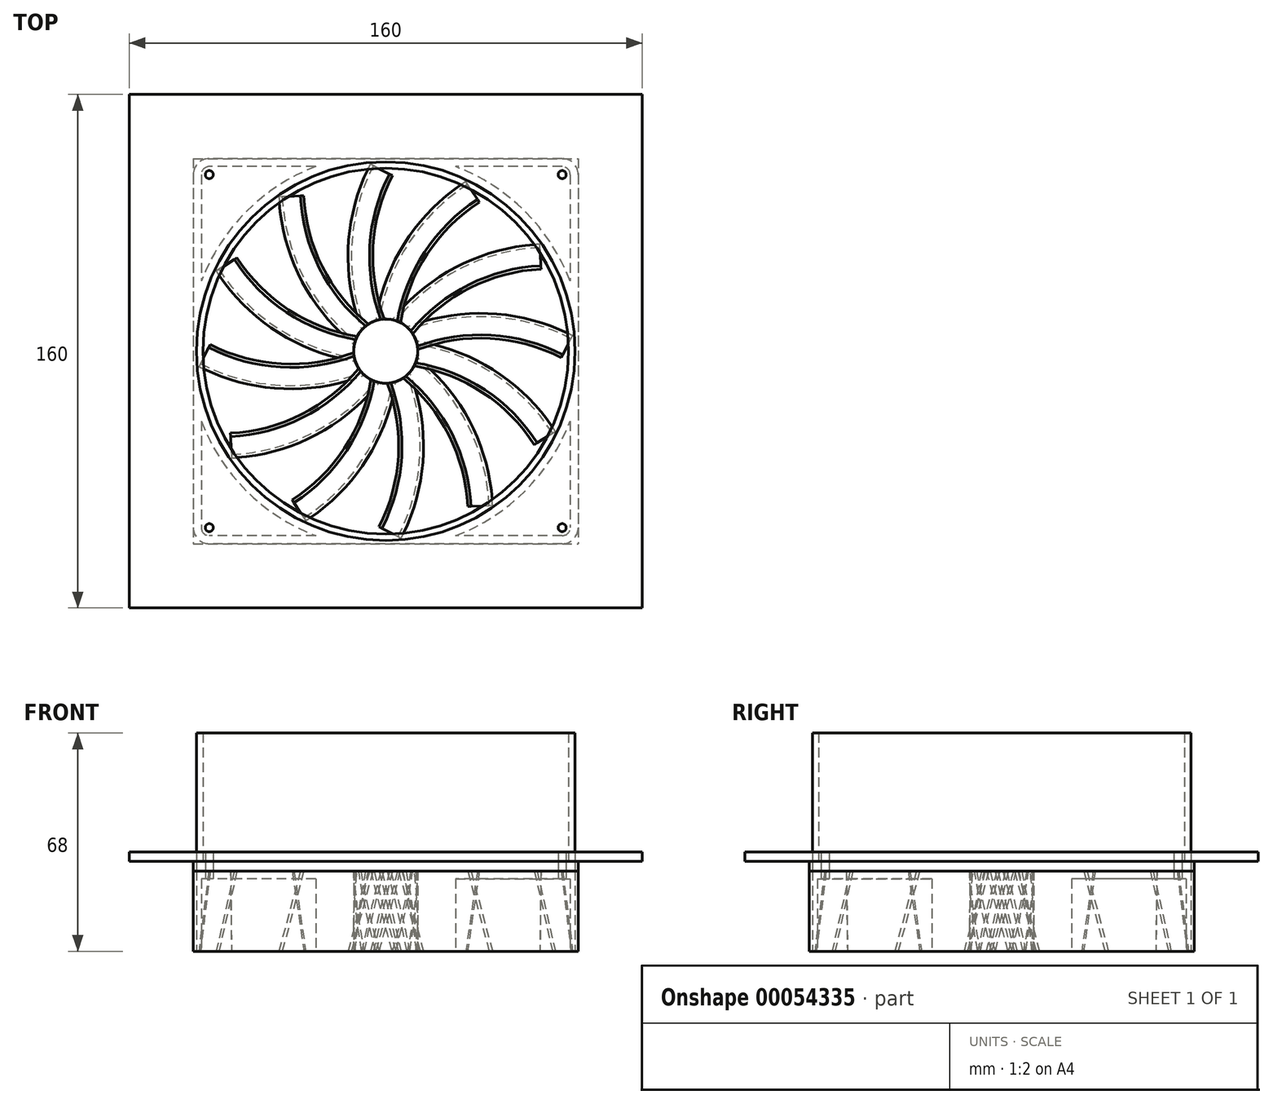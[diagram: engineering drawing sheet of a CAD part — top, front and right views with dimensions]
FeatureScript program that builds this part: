
annotation { "Feature Type Name" : "Feature", "Feature Type Description" : "" }
export const myFeature = defineFeature(function(context is Context, id is Id, definition is map)
    precondition{}
    {
        {
            var Q0;
            Q0=qCreatedBy(makeId("Top.planeOp"),FACE);
            var sketch = newSketch(context, id + "F0", { "sketchPlane" : qUnion([Q0])});
            skCircle(sketch, "E0", {"center": v(0, 0) * mm, "radius": 59 * mm});
            skCircle(sketch, "E1", {"center": v(0, 0) * mm, "radius": 10 * mm});
            skLineSegment(sketch, "E2", {"start": v(0, 0) * mm, "end": v(0, 59) * mm, "construction": true});
            skArc(sketch, "E3", {"start": v(27.05, 49.6) * mm, "mid": v(7.2, 28.25) * mm, "end": v(0, 0) * mm});
            skLineSegment(sketch, "E4.rect.bottom", {"start": v(60, 60) * mm, "end": v(-60, 60) * mm});
            skLineSegment(sketch, "E4.rect.top", {"start": v(60, -60) * mm, "end": v(-60, -60) * mm});
            skLineSegment(sketch, "E4.rect.left", {"start": v(60, 60) * mm, "end": v(60, -60) * mm});
            skLineSegment(sketch, "E4.rect.right", {"start": v(-60, 60) * mm, "end": v(-60, -60) * mm});
            skCircle(sketch, "E5", {"center": v(0, 0) * mm, "radius": 56.5 * mm, "construction": true});
            skPoint(sketch, "E6", {"position": v(-55, -55) * mm});
            skPoint(sketch, "E7", {"position": v(55, -55) * mm});
            skPoint(sketch, "E8", {"position": v(55, 55) * mm});
            skPoint(sketch, "E9", {"position": v(-55, 55) * mm});
            skSolve(sketch);
        }
        {
            var Q0;
            Q0=makeQuery(id+"F0.imprint","IMPRINT",FACE,{"disambiguationData":[TD([[makeQuery(id+"F0.imprint","IMPRINT",EDGE,{"derivedFrom":sQuery(id+"F0.wireOp",EDGE,"E1")}),1.0]])]});
            var Q1;
            Q1=sQuery(id+"F0.wireOp",EDGE,"E1");
            extrude(context, id + "F1", {"entities" : qUnion([Q0]), "surfaceEntities" : qUnion([Q1]), "depth" : (25 / 2) * mm, "hasSecondDirection" : true, "secondDirectionOppositeDirection" : true, "secondDirectionDepth" : (25 / 2) * mm});
        }
        {
            var Q0;
            Q0=makeQuery(id+"F0.imprint","IMPRINT",FACE,{"disambiguationData":[TD([[makeQuery(id+"F0.imprint","IMPRINT",EDGE,{"derivedFrom":sQuery(id+"F0.wireOp",EDGE,"E0")}),-1.0]])]});
            extrude(context, id + "F2", {"entities" : qUnion([Q0]), "depth" : (25 / 2) * mm, "hasSecondDirection" : true, "secondDirectionOppositeDirection" : true, "secondDirectionDepth" : (25 / 2) * mm});
        }
        {
            var Q0;
            Q0=makeQuery(id+"F2.opExtrude","SWEPT_EDGE",EDGE,{"disambiguationData":[OSD([sQuery(id+"F0.wireOp",EDGE,"E4.rect.top"),sQuery(id+"F0.wireOp",EDGE,"E4.rect.left")])]});
            var Q1;
            Q1=makeQuery(id+"F2.opExtrude","SWEPT_EDGE",EDGE,{"disambiguationData":[OSD([sQuery(id+"F0.wireOp",EDGE,"E4.rect.top"),sQuery(id+"F0.wireOp",EDGE,"E4.rect.right")])]});
            var Q2;
            Q2=makeQuery(id+"F2.opExtrude","SWEPT_EDGE",EDGE,{"disambiguationData":[OSD([sQuery(id+"F0.wireOp",EDGE,"E4.rect.bottom"),sQuery(id+"F0.wireOp",EDGE,"E4.rect.right")])]});
            var Q3;
            Q3=makeQuery(id+"F2.opExtrude","SWEPT_EDGE",EDGE,{"disambiguationData":[OSD([sQuery(id+"F0.wireOp",EDGE,"E4.rect.bottom"),sQuery(id+"F0.wireOp",EDGE,"E4.rect.left")])]});
            fillet(context, id + "F3", {"entities" : qUnion([Q0, Q1, Q2, Q3]), "radius" : 5 * mm, "tangentPropagation" : true, "allowEdgeOverflow" : false});
        }
        {
            var Q0;
            Q0=makeQuery(id+"F2.opExtrude","CAP_FACE",FACE,{"disambiguationData":[OSD([sQuery(id+"F0.wireOp",EDGE,"E0"),sQuery(id+"F0.wireOp",EDGE,"E4.rect.bottom"),sQuery(id+"F0.wireOp",EDGE,"E4.rect.top"),sQuery(id+"F0.wireOp",EDGE,"E4.rect.left"),sQuery(id+"F0.wireOp",EDGE,"E4.rect.right")])],"isStart":true});
            shell(context, id + "F4", {"entities" : qUnion([Q0]), "thickness" : 2.5 * mm});
        }
        {
            var Q0;
            Q0=sQuery(id+"F0.wireOp",VERTEX,"E6");
            var Q1;
            Q1=sQuery(id+"F0.wireOp",VERTEX,"E7");
            var Q2;
            Q2=sQuery(id+"F0.wireOp",VERTEX,"E8");
            var Q3;
            Q3=sQuery(id+"F0.wireOp",VERTEX,"E9");
            var Q4;
            Q4=makeQuery(id+"F2.opExtrude","SWEPT_BODY",BODY,{"disambiguationData":[OSD([sQuery(id+"F0.wireOp",EDGE,"E0"),sQuery(id+"F0.wireOp",EDGE,"E4.rect.bottom"),sQuery(id+"F0.wireOp",EDGE,"E4.rect.top"),sQuery(id+"F0.wireOp",EDGE,"E4.rect.left"),sQuery(id+"F0.wireOp",EDGE,"E4.rect.right")])]});
            hole(context, id + "F5", {"style" : HoleStyle.SIMPLE, "holeDiameter" : 2.5 * mm, "endStyle" : HoleEndStyle.THROUGH, "oppositeDirection" : true, "locations" : qUnion([Q0, Q1, Q2, Q3]), "scope" : qUnion([Q4])});
        }
        {
            var Q0;
            Q0=qCreatedBy(makeId("Front.planeOp"),FACE);
            var sketch = newSketch(context, id + "F6", { "sketchPlane" : qUnion([Q0])});
            skLineSegment(sketch, "E10", {"start": v(3.35, 12.5) * mm, "end": v(-3.35, -12.5) * mm, "construction": true});
            skLineSegment(sketch, "E11.0", {"start": v(2.83, 12.5) * mm, "end": v(-3.87, -12.5) * mm});
            skLineSegment(sketch, "E12.0", {"start": v(3.87, 12.5) * mm, "end": v(-2.83, -12.5) * mm});
            skLineSegment(sketch, "E13", {"start": v(-2.83, -12.5) * mm, "end": v(-3.87, -12.5) * mm});
            skLineSegment(sketch, "E14", {"start": v(3.87, 12.5) * mm, "end": v(2.83, 12.5) * mm});
            skSolve(sketch);
        }
        {
            var Q0;
            Q0=makeQuery(id+"F6.imprint","IMPRINT",FACE,{"disambiguationData":[TD([[makeQuery(id+"F6.imprint","IMPRINT",EDGE,{"derivedFrom":sQuery(id+"F6.wireOp",EDGE,"E11.0")}),1.0]])]});
            var Q1;
            Q1=sQuery(id+"F0.wireOp",EDGE,"E3");
            sweep(context, id + "F7", {"operationType" : NewBodyOperationType.ADD, "profiles" : qUnion([Q0]), "path" : qUnion([Q1])});
        }
        {
            var Q0;
            Q0=makeQuery(id+"F1.opExtrude","SWEPT_BODY",BODY,{"disambiguationData":[OSD([sQuery(id+"F0.wireOp",EDGE,"E1")])]});
            var Q1;
            Q1=makeQuery(id+"F2.opExtrude","CAP_EDGE",EDGE,{"disambiguationData":[OSD([sQuery(id+"F0.wireOp",EDGE,"E0")])],"isStart":true});
            circularPattern(context, id + "F8", {"operationType" : NewBodyOperationType.ADD, "entities" : qUnion([Q0]), "axis" : qUnion([Q1]), "angle" : 30 * degree, "instanceCount" : 12});
        }
        {
            var Q0;
            Q0=makeQuery(id+"F2.opExtrude","CAP_FACE",FACE,{"disambiguationData":[OSD([sQuery(id+"F0.wireOp",EDGE,"E0"),sQuery(id+"F0.wireOp",EDGE,"E4.rect.bottom"),sQuery(id+"F0.wireOp",EDGE,"E4.rect.top"),sQuery(id+"F0.wireOp",EDGE,"E4.rect.left"),sQuery(id+"F0.wireOp",EDGE,"E4.rect.right")])],"isStart":false});
            var sketch = newSketch(context, id + "F9", { "sketchPlane" : qUnion([Q0])});
            skPoint(sketch, "E15.middle", {"position": v(0, 0) * mm});
            skLineSegment(sketch, "E16.bottom", {"start": v(-60, 60) * mm, "end": v(60, 60) * mm});
            skLineSegment(sketch, "E16.top", {"start": v(-60, -60) * mm, "end": v(60, -60) * mm});
            skLineSegment(sketch, "E16.left", {"start": v(-60, 60) * mm, "end": v(-60, -60) * mm});
            skLineSegment(sketch, "E16.right", {"start": v(60, 60) * mm, "end": v(60, -60) * mm});
            skSolve(sketch);
        }
        {
            var Q0;
            Q0=makeQuery(id+"F9.imprint","IMPRINT",FACE,{"disambiguationData":[TD([[makeQuery(id+"F9.imprint","IMPRINT",EDGE,{"derivedFrom":makeQuery(id+"F5.hole-0.boolean.opBoolean","INTERSECT",EDGE,{"derivedFrom":[makeQuery(id+"F2.opExtrude","CAP_FACE",FACE,{"disambiguationData":[OSD([sQuery(id+"F0.wireOp",EDGE,"E0"),sQuery(id+"F0.wireOp",EDGE,"E4.rect.bottom"),sQuery(id+"F0.wireOp",EDGE,"E4.rect.top"),sQuery(id+"F0.wireOp",EDGE,"E4.rect.left"),sQuery(id+"F0.wireOp",EDGE,"E4.rect.right")])],"isStart":false}),makeQuery(id+"F5.hole-0.opRevolve","SWEPT_FACE",FACE,{"disambiguationData":[OSD([sQuery(id+"F5.hole-0.sketch.wireOp",EDGE,"core_line_2")])]})]})}),-1.0]])]});
            var Q1;
            Q1=makeQuery(id+"F9.imprint","IMPRINT",FACE,{"disambiguationData":[TD([[makeQuery(id+"F9.imprint","IMPRINT",EDGE,{"derivedFrom":makeQuery(id+"F5.hole-1.boolean.opBoolean","INTERSECT",EDGE,{"derivedFrom":[makeQuery(id+"F2.opExtrude","CAP_FACE",FACE,{"disambiguationData":[OSD([sQuery(id+"F0.wireOp",EDGE,"E0"),sQuery(id+"F0.wireOp",EDGE,"E4.rect.bottom"),sQuery(id+"F0.wireOp",EDGE,"E4.rect.top"),sQuery(id+"F0.wireOp",EDGE,"E4.rect.left"),sQuery(id+"F0.wireOp",EDGE,"E4.rect.right")])],"isStart":false}),makeQuery(id+"F5.hole-1.opRevolve","SWEPT_FACE",FACE,{"disambiguationData":[OSD([sQuery(id+"F5.hole-1.sketch.wireOp",EDGE,"core_line_2")])]})]})}),-1.0]])]});
            var Q2;
            Q2=makeQuery(id+"F9.imprint","IMPRINT",FACE,{"disambiguationData":[TD([[makeQuery(id+"F9.imprint","IMPRINT",EDGE,{"derivedFrom":makeQuery(id+"F5.hole-2.boolean.opBoolean","INTERSECT",EDGE,{"derivedFrom":[makeQuery(id+"F2.opExtrude","CAP_FACE",FACE,{"disambiguationData":[OSD([sQuery(id+"F0.wireOp",EDGE,"E0"),sQuery(id+"F0.wireOp",EDGE,"E4.rect.bottom"),sQuery(id+"F0.wireOp",EDGE,"E4.rect.top"),sQuery(id+"F0.wireOp",EDGE,"E4.rect.left"),sQuery(id+"F0.wireOp",EDGE,"E4.rect.right")])],"isStart":false}),makeQuery(id+"F5.hole-2.opRevolve","SWEPT_FACE",FACE,{"disambiguationData":[OSD([sQuery(id+"F5.hole-2.sketch.wireOp",EDGE,"core_line_2")])]})]})}),-1.0]])]});
            var Q3;
            {var subQ1=sQuery(id+"F0.wireOp",EDGE,"E4.rect.right");var subQ2=sQuery(id+"F0.wireOp",EDGE,"E4.rect.bottom");var subQ3=makeQuery(id+"F3.opFillet","BLEND_EDGE",EDGE,{"blendedFrom":[makeQuery(id+"F2.opExtrude","SWEPT_EDGE",EDGE,{"disambiguationData":[OSD([subQ2,subQ1])]}),makeQuery(id+"F2.opExtrude","CAP_FACE",FACE,{"disambiguationData":[OSD([sQuery(id+"F0.wireOp",EDGE,"E0"),subQ2,sQuery(id+"F0.wireOp",EDGE,"E4.rect.top"),sQuery(id+"F0.wireOp",EDGE,"E4.rect.left"),subQ1])],"isStart":false})],"blendedInto":[makeQuery(id+"F2.opExtrude","CAP_FACE",FACE,{"disambiguationData":[OSD([sQuery(id+"F0.wireOp",EDGE,"E0"),subQ2,sQuery(id+"F0.wireOp",EDGE,"E4.rect.top"),sQuery(id+"F0.wireOp",EDGE,"E4.rect.left"),subQ1])],"isStart":false})]});Q3=makeQuery(id+"F9.imprint","IMPRINT",FACE,{"disambiguationData":[TD([[makeQuery(id+"F9.imprint","IMPRINT",EDGE,{"derivedFrom":subQ3}),-1.0]])]});}
            var Q4;
            {var subQ1=sQuery(id+"F0.wireOp",EDGE,"E4.rect.right");var subQ2=sQuery(id+"F0.wireOp",EDGE,"E4.rect.top");var subQ3=makeQuery(id+"F3.opFillet","BLEND_EDGE",EDGE,{"blendedFrom":[makeQuery(id+"F2.opExtrude","SWEPT_EDGE",EDGE,{"disambiguationData":[OSD([subQ2,subQ1])]}),makeQuery(id+"F2.opExtrude","CAP_FACE",FACE,{"disambiguationData":[OSD([sQuery(id+"F0.wireOp",EDGE,"E0"),sQuery(id+"F0.wireOp",EDGE,"E4.rect.bottom"),subQ2,sQuery(id+"F0.wireOp",EDGE,"E4.rect.left"),subQ1])],"isStart":false})],"blendedInto":[makeQuery(id+"F2.opExtrude","CAP_FACE",FACE,{"disambiguationData":[OSD([sQuery(id+"F0.wireOp",EDGE,"E0"),sQuery(id+"F0.wireOp",EDGE,"E4.rect.bottom"),subQ2,sQuery(id+"F0.wireOp",EDGE,"E4.rect.left"),subQ1])],"isStart":false})]});Q4=makeQuery(id+"F9.imprint","IMPRINT",FACE,{"disambiguationData":[TD([[makeQuery(id+"F9.imprint","IMPRINT",EDGE,{"derivedFrom":subQ3}),-1.0]])]});}
            var Q5;
            {var subQ1=sQuery(id+"F0.wireOp",EDGE,"E4.rect.left");var subQ2=sQuery(id+"F0.wireOp",EDGE,"E4.rect.top");var subQ3=makeQuery(id+"F3.opFillet","BLEND_EDGE",EDGE,{"blendedFrom":[makeQuery(id+"F2.opExtrude","SWEPT_EDGE",EDGE,{"disambiguationData":[OSD([subQ2,subQ1])]}),makeQuery(id+"F2.opExtrude","CAP_FACE",FACE,{"disambiguationData":[OSD([sQuery(id+"F0.wireOp",EDGE,"E0"),sQuery(id+"F0.wireOp",EDGE,"E4.rect.bottom"),subQ2,subQ1,sQuery(id+"F0.wireOp",EDGE,"E4.rect.right")])],"isStart":false})],"blendedInto":[makeQuery(id+"F2.opExtrude","CAP_FACE",FACE,{"disambiguationData":[OSD([sQuery(id+"F0.wireOp",EDGE,"E0"),sQuery(id+"F0.wireOp",EDGE,"E4.rect.bottom"),subQ2,subQ1,sQuery(id+"F0.wireOp",EDGE,"E4.rect.right")])],"isStart":false})]});Q5=makeQuery(id+"F9.imprint","IMPRINT",FACE,{"disambiguationData":[TD([[makeQuery(id+"F9.imprint","IMPRINT",EDGE,{"derivedFrom":subQ3}),-1.0]])]});}
            var Q6;
            {var subQ1=sQuery(id+"F0.wireOp",EDGE,"E4.rect.left");var subQ2=sQuery(id+"F0.wireOp",EDGE,"E4.rect.bottom");var subQ3=makeQuery(id+"F3.opFillet","BLEND_EDGE",EDGE,{"blendedFrom":[makeQuery(id+"F2.opExtrude","SWEPT_EDGE",EDGE,{"disambiguationData":[OSD([subQ2,subQ1])]}),makeQuery(id+"F2.opExtrude","CAP_FACE",FACE,{"disambiguationData":[OSD([sQuery(id+"F0.wireOp",EDGE,"E0"),subQ2,sQuery(id+"F0.wireOp",EDGE,"E4.rect.top"),subQ1,sQuery(id+"F0.wireOp",EDGE,"E4.rect.right")])],"isStart":false})],"blendedInto":[makeQuery(id+"F2.opExtrude","CAP_FACE",FACE,{"disambiguationData":[OSD([sQuery(id+"F0.wireOp",EDGE,"E0"),subQ2,sQuery(id+"F0.wireOp",EDGE,"E4.rect.top"),subQ1,sQuery(id+"F0.wireOp",EDGE,"E4.rect.right")])],"isStart":false})]});Q6=makeQuery(id+"F9.imprint","IMPRINT",FACE,{"disambiguationData":[TD([[makeQuery(id+"F9.imprint","IMPRINT",EDGE,{"derivedFrom":subQ3}),-1.0]])]});}
            var Q7;
            {var subQ4=sQuery(id+"F0.wireOp",EDGE,"E0");Q7=makeQuery(id+"F9.imprint","IMPRINT",FACE,{"disambiguationData":[TD([[makeQuery(id+"F9.imprint","IMPRINT",EDGE,{"derivedFrom":makeQuery(id+"F2.opExtrude","CAP_EDGE",EDGE,{"disambiguationData":[OSD([subQ4])],"isStart":false})}),-1.0]])]});}
            var Q8;
            Q8=makeQuery(id+"F9.imprint","IMPRINT",FACE,{"disambiguationData":[TD([[makeQuery(id+"F9.imprint","IMPRINT",EDGE,{"derivedFrom":makeQuery(id+"F5.hole-3.boolean.opBoolean","INTERSECT",EDGE,{"derivedFrom":[makeQuery(id+"F2.opExtrude","CAP_FACE",FACE,{"disambiguationData":[OSD([sQuery(id+"F0.wireOp",EDGE,"E0"),sQuery(id+"F0.wireOp",EDGE,"E4.rect.bottom"),sQuery(id+"F0.wireOp",EDGE,"E4.rect.top"),sQuery(id+"F0.wireOp",EDGE,"E4.rect.left"),sQuery(id+"F0.wireOp",EDGE,"E4.rect.right")])],"isStart":false}),makeQuery(id+"F5.hole-3.opRevolve","SWEPT_FACE",FACE,{"disambiguationData":[OSD([sQuery(id+"F5.hole-3.sketch.wireOp",EDGE,"core_line_2")])]})]})}),-1.0]])]});
            extrude(context, id + "F10", {"entities" : qUnion([Q0, Q1, Q2, Q3, Q4, Q5, Q6, Q7, Q8]), "depth" : 3 * mm});
        }
        {
            var Q0;
            Q0=makeQuery(id+"F10.opExtrude","CAP_FACE",FACE,{"disambiguationData":[OSD([sQuery(id+"F0.wireOp",EDGE,"E0"),sQuery(id+"F9.wireOp",EDGE,"E16.bottom"),sQuery(id+"F9.wireOp",EDGE,"E16.top"),sQuery(id+"F9.wireOp",EDGE,"E16.left"),sQuery(id+"F9.wireOp",EDGE,"E16.right")])],"isStart":false});
            var sketch = newSketch(context, id + "F11", { "sketchPlane" : qUnion([Q0])});
            skLineSegment(sketch, "E17.bottom", {"start": v(-80, 80) * mm, "end": v(80, 80) * mm});
            skLineSegment(sketch, "E17.top", {"start": v(-80, -80) * mm, "end": v(80, -80) * mm});
            skLineSegment(sketch, "E17.left", {"start": v(-80, 80) * mm, "end": v(-80, -80) * mm});
            skLineSegment(sketch, "E17.right", {"start": v(80, 80) * mm, "end": v(80, -80) * mm});
            skPoint(sketch, "E17.middle", {"position": v(0, 0) * mm});
            skSolve(sketch);
        }
        {
            var Q0;
            Q0=makeQuery(id+"F11.imprint","IMPRINT",FACE,{"disambiguationData":[TD([[makeQuery(id+"F11.imprint","IMPRINT",EDGE,{"derivedFrom":sQuery(id+"F11.wireOp",EDGE,"E17.bottom")}),-1.0]])]});
            var Q1;
            Q1=makeQuery(id+"F11.imprint","IMPRINT",FACE,{"disambiguationData":[TD([[makeQuery(id+"F11.imprint","IMPRINT",EDGE,{"derivedFrom":makeQuery(id+"F10.opExtrude","CAP_EDGE",EDGE,{"disambiguationData":[OSD([sQuery(id+"F9.wireOp",EDGE,"E16.bottom")])],"isStart":false})}),-1.0]])]});
            extrude(context, id + "F12", {"entities" : qUnion([Q0, Q1]), "depth" : 3 * mm});
        }
        {
            var Q0;
            Q0=makeQuery(id+"F12.opExtrude","CAP_FACE",FACE,{"disambiguationData":[OSD([sQuery(id+"F0.wireOp",EDGE,"E0"),sQuery(id+"F11.wireOp",EDGE,"E17.bottom"),sQuery(id+"F11.wireOp",EDGE,"E17.top"),sQuery(id+"F11.wireOp",EDGE,"E17.left"),sQuery(id+"F11.wireOp",EDGE,"E17.right")])],"isStart":true});
            var sketch = newSketch(context, id + "F13", { "sketchPlane" : qUnion([Q0])});
            skCircle(sketch, "E18", {"center": v(0, 0) * mm, "radius": 59 * mm});
            skCircle(sketch, "E19", {"center": v(0, 0) * mm, "radius": 57 * mm});
            skSolve(sketch);
        }
        {
            var Q0;
            Q0=makeQuery(id+"F13.imprint","IMPRINT",FACE,{"disambiguationData":[TD([[makeQuery(id+"F13.imprint","IMPRINT",EDGE,{"derivedFrom":sQuery(id+"F13.wireOp",EDGE,"E18")}),-1.0]])]});
            extrude(context, id + "F14", {"entities" : qUnion([Q0]), "oppositeDirection" : true, "depth" : 40 * mm});
        }
    });
